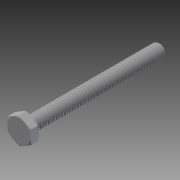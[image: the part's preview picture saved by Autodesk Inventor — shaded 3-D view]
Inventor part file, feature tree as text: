
AUTODESK INVENTOR PART (.ipt)
format: ipt  version: 2014 SP1 (Build 180222100, 222)  size: 979,968 bytes
history: native  units: in
note: dims shown in document units (in); Inventor stores cm internally (conversion verified against a paired STEP export)
features: extrude x1, other x1, imported_body x1
ambient origin geometry x8: Origin, YZ Plane, XZ Plane, XY Plane, X Axis, Y Axis, Z Axis, Center Point
bodies: Body1 (feature_tree)
feature tree (3):
  extrude  "Extrude14"  [1 undecoded]
  other  "92620A5521"
  imported_body  "Base1"
note: 1 required parameter value undecoded (feature->parameter linkage not recoverable at this tier; creation-order binding heuristic only, values carry confidence <= 0.55)
